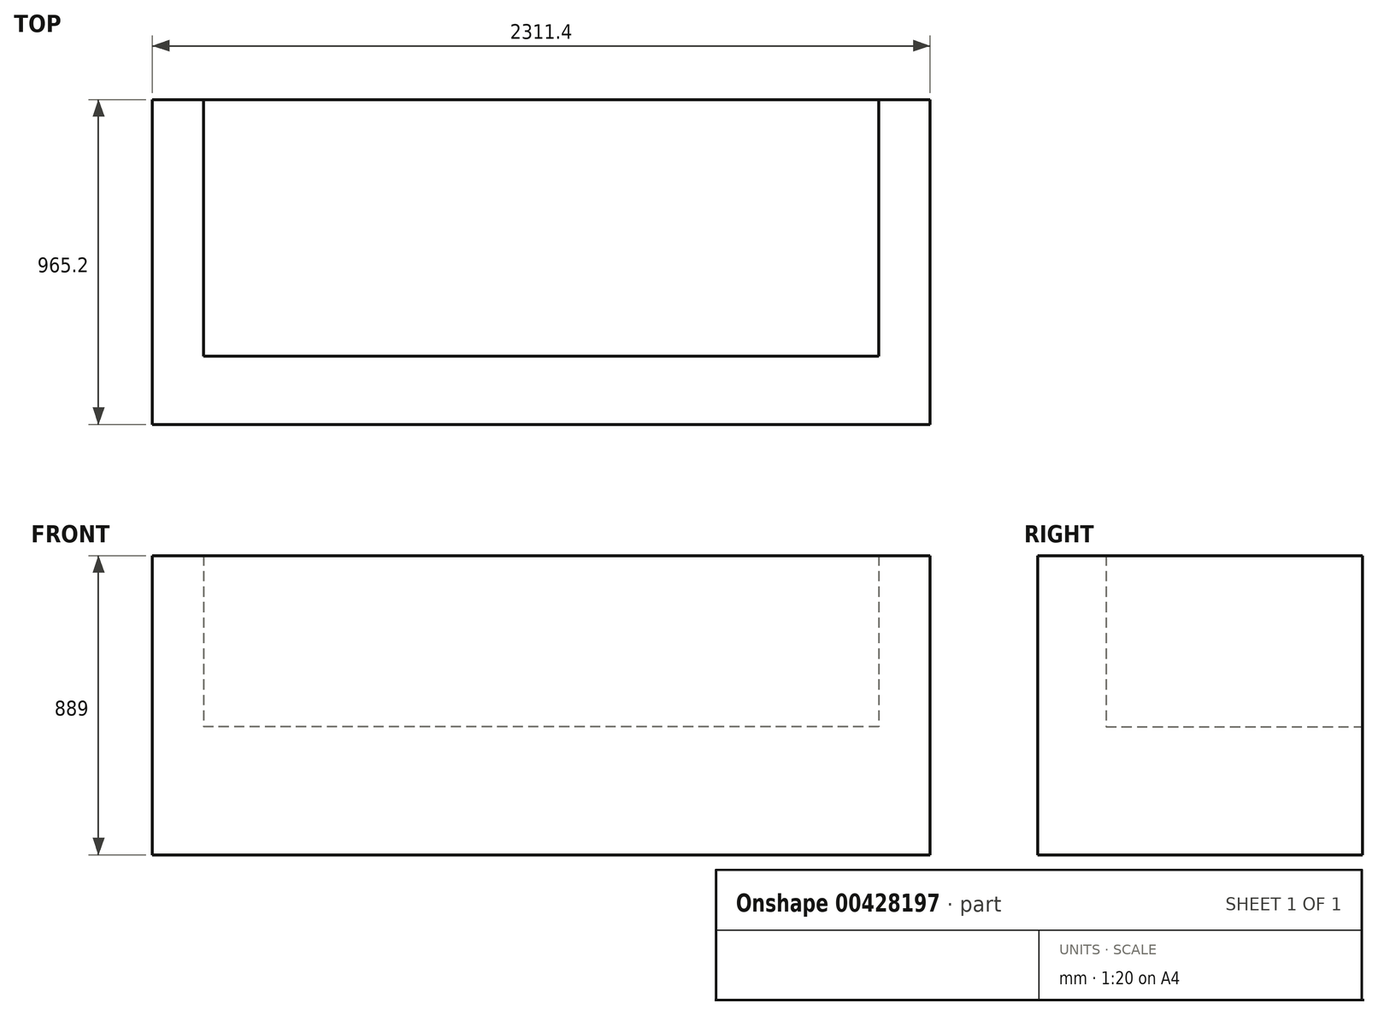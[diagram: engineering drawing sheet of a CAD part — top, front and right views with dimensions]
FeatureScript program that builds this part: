
annotation { "Feature Type Name" : "Feature", "Feature Type Description" : "" }
export const myFeature = defineFeature(function(context is Context, id is Id, definition is map)
    precondition{}
    {
        {
            var Q0;
            Q0=qCreatedBy(makeId("Front.planeOp"),FACE);
            var sketch = newSketch(context, id + "F0", { "sketchPlane" : qUnion([Q0])});
            skLineSegment(sketch, "E0.bottom", {"start": v(-1155.7, -444.5) * mm, "end": v(1155.7, -444.5) * mm});
            skLineSegment(sketch, "E0.top", {"start": v(-1155.7, 444.5) * mm, "end": v(1155.7, 444.5) * mm});
            skLineSegment(sketch, "E0.left", {"start": v(-1155.7, -444.5) * mm, "end": v(-1155.7, 444.5) * mm});
            skLineSegment(sketch, "E0.right", {"start": v(1155.7, -444.5) * mm, "end": v(1155.7, 444.5) * mm});
            skPoint(sketch, "E0.middle", {"position": v(0, 0) * mm});
            skSolve(sketch);
        }
        {
            var Q0;
            Q0=makeQuery(id+"F0.imprint","IMPRINT",FACE,{"disambiguationData":[TD([[makeQuery(id+"F0.imprint","IMPRINT",EDGE,{"derivedFrom":sQuery(id+"F0.wireOp",EDGE,"E0.bottom")}),1.0]])]});
            extrude(context, id + "F1", {"entities" : qUnion([Q0]), "depth" : 965.2 * mm});
        }
        {
            var Q0;
            Q0=makeQuery(id+"F1.opExtrude","CAP_FACE",FACE,{"disambiguationData":[OSD([sQuery(id+"F0.wireOp",EDGE,"E0.bottom"),sQuery(id+"F0.wireOp",EDGE,"E0.top"),sQuery(id+"F0.wireOp",EDGE,"E0.left"),sQuery(id+"F0.wireOp",EDGE,"E0.right")])],"isStart":true});
            var sketch = newSketch(context, id + "F2", { "sketchPlane" : qUnion([Q0])});
            skLineSegment(sketch, "E1.bottom", {"start": v(-1003.3, 444.5) * mm, "end": v(1003.3, 444.5) * mm});
            skLineSegment(sketch, "E1.top", {"start": v(-1003.3, -63.5) * mm, "end": v(1003.3, -63.5) * mm});
            skLineSegment(sketch, "E1.left", {"start": v(-1003.3, 444.5) * mm, "end": v(-1003.3, -63.5) * mm});
            skLineSegment(sketch, "E1.right", {"start": v(1003.3, 444.5) * mm, "end": v(1003.3, -63.5) * mm});
            skSolve(sketch);
        }
        {
            var Q0;
            Q0=makeQuery(id+"F2.imprint","IMPRINT",FACE,{"disambiguationData":[TD([[makeQuery(id+"F2.imprint","IMPRINT",EDGE,{"derivedFrom":sQuery(id+"F2.wireOp",EDGE,"E1.bottom")}),1.0]])]});
            extrude(context, id + "F3", {"entities" : qUnion([Q0]), "operationType" : NewBodyOperationType.REMOVE, "oppositeDirection" : true, "depth" : 762 * mm});
        }
    });
